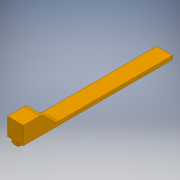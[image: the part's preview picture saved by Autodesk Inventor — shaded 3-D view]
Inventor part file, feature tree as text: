
AUTODESK INVENTOR PART (.ipt)
format: ipt  version: 2017 (Build 210142000, 142)  size: 225,792 bytes
history: native  units: in
note: dims shown in document units (in); Inventor stores cm internally (conversion verified against a paired STEP export)
features: sketch x7, extrude x6, fillet x3, other x1, plane x1, chamfer x1
ambient origin geometry x8: Origin, YZ Plane, XZ Plane, XY Plane, X Axis, Y Axis, Z Axis, Center Point
bodies: Solid1 (feature_tree)
feature tree (19):
  other  "20X20Connector"
  extrude  "Extrusion1"  Depth=1.0in
  plane  "Work Plane1"
  fillet  "Fillet2"  Radius=1.0in
  extrude  "Extrusion2"  Depth=7.0in TaperAngle=0.0deg
  sketch  "Sketch3"  dims[d22=0.1in d23=0.0in d24=0.0156in d25=1.0in]
  extrude  "Extrusion3"  Depth=0.0156in
  fillet  "Fillet3"  Radius=1.0in
  extrude  "Extrusion4"  Depth=0.75in TaperAngle=45.0deg
  chamfer  "Chamfer1"  Distance=0.1in
  extrude  "Extrusion5"  Depth=0.25in
  extrude  "Extrusion6"  [1 undecoded]
  fillet  "Fillet4"  [1 undecoded]
  sketch  "Sketch1"  dims[d0=0.0984in d1=0.0787in d2=0.1874in d3=0.4524in d4=0.1085in d5=0.225in d6=0.2221in d7=0.2313in d8=0.03in d9=0.03in d11=0.9949in d12=0.1137in d13=0.6693in d14=0.65in d15=1.0in d16=0.0in]
  sketch  "Sketch2"  dims[d17=0.0in d19=0.0156in d20=7.0in d21=0.0in]
  sketch  "Sketch4"  dims[d26=0.75in d27=0.0in d28=0.75in d29=0.125in d30=45.0deg d31=0.1in d32=0.0in]
  sketch  "Sketch5"  dims[d33=0.1in d34=0.0in d35=0.25in]
  sketch  "Sketch6"
  sketch  "Sketch7"
note: 2 required parameter values undecoded (feature->parameter linkage not recoverable at this tier; creation-order binding heuristic only, values carry confidence <= 0.55)
